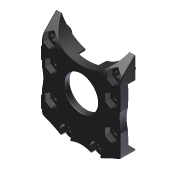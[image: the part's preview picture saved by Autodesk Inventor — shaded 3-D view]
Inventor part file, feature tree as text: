
AUTODESK INVENTOR PART (.ipt)
format: ipt  version: 2015 (Build 190159000, 159)  size: 4,061,184 bytes
history: native  units: in
note: dims shown in document units (in); Inventor stores cm internally (conversion verified against a paired STEP export)
features: chamfer x1, other x1, imported_body x1
ambient origin geometry x8: Origin, YZ Plane, XZ Plane, XY Plane, X Axis, Y Axis, Z Axis, Center Point
bodies: Body1 (feature_tree)
feature tree (3):
  chamfer  "Chamfer3"  [1 undecoded]
  other  "217-4156-002 Rev5.ipt1"
  imported_body  "Base1"
note: 1 required parameter value undecoded (feature->parameter linkage not recoverable at this tier; creation-order binding heuristic only, values carry confidence <= 0.55)
